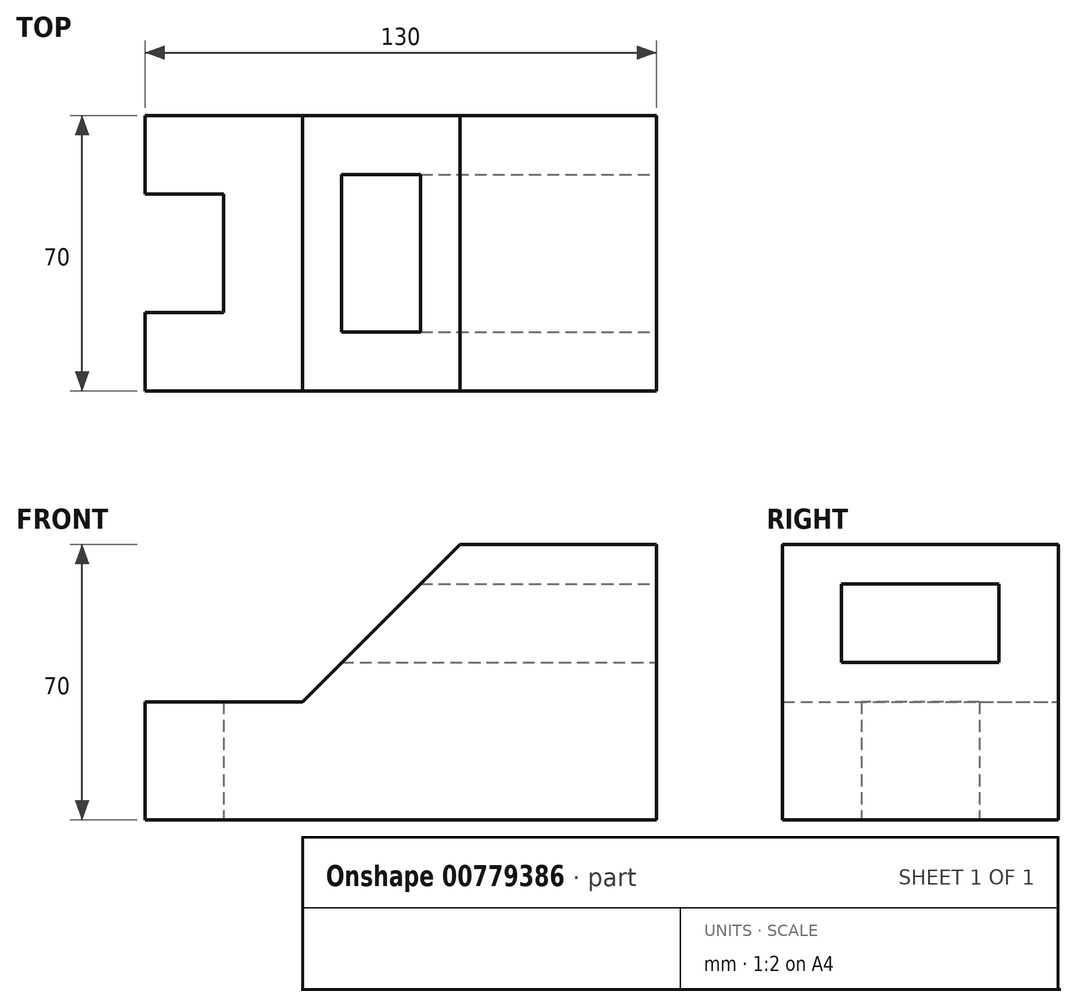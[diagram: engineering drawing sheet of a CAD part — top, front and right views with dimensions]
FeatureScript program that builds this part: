
annotation { "Feature Type Name" : "Feature", "Feature Type Description" : "" }
export const myFeature = defineFeature(function(context is Context, id is Id, definition is map)
    precondition{}
    {
        {
            var Q0;
            Q0=qCreatedBy(makeId("Front.planeOp"),FACE);
            var sketch = newSketch(context, id + "F0", { "sketchPlane" : qUnion([Q0])});
            skLineSegment(sketch, "E0.bottom", {"start": v(65, 35) * mm, "end": v(15, 35) * mm});
            skLineSegment(sketch, "E0.top", {"start": v(65, -35) * mm, "end": v(-65, -35) * mm});
            skLineSegment(sketch, "E0.left", {"start": v(65, 35) * mm, "end": v(65, -35) * mm});
            skLineSegment(sketch, "E0.right", {"start": v(-65, -5) * mm, "end": v(-65, -35) * mm});
            skPoint(sketch, "E0.middle", {"position": v(0, 0) * mm});
            skLineSegment(sketch, "E1.bottom", {"start": v(-65, -35) * mm, "end": v(-25, -35) * mm});
            skLineSegment(sketch, "E1.top", {"start": v(-65, -5) * mm, "end": v(-25, -5) * mm});
            skLineSegment(sketch, "E1.left", {"start": v(-65, -35) * mm, "end": v(-65, -5) * mm});
            skLineSegment(sketch, "E2", {"start": v(-25, -5) * mm, "end": v(15, 35) * mm});
            skPoint(sketch, "E3.orphan", {"position": v(-65, 35) * mm});
            skSolve(sketch);
        }
        {
            var Q0;
            Q0 = qSketchRegion(id + "F0", true);
            extrude(context, id + "F1", {"entities" : qUnion([Q0]), "depth" : 70 * mm, "offsetDistance" : 25 * mm});
        }
        {
            var Q0;
            Q0=makeQuery(id+"F1.opExtrude","SWEPT_FACE",FACE,{"disambiguationData":[OSD([sQuery(id+"F0.wireOp",EDGE,"E0.top"),sQuery(id+"F0.wireOp",EDGE,"E1.bottom")])]});
            var sketch = newSketch(context, id + "F2", { "sketchPlane" : qUnion([Q0])});
            skLineSegment(sketch, "E4.bottom", {"start": v(-65, 70) * mm, "end": v(-45, 70) * mm});
            skLineSegment(sketch, "E4.top", {"start": v(-65, 50) * mm, "end": v(-45, 50) * mm});
            skLineSegment(sketch, "E4.left", {"start": v(-65, 70) * mm, "end": v(-65, 50) * mm});
            skLineSegment(sketch, "E4.right", {"start": v(-45, 70) * mm, "end": v(-45, 50) * mm});
            skLineSegment(sketch, "E5.bottom", {"start": v(-65, 0) * mm, "end": v(-45, 0) * mm});
            skLineSegment(sketch, "E5.top", {"start": v(-65, 20) * mm, "end": v(-45, 20) * mm});
            skLineSegment(sketch, "E5.left", {"start": v(-65, 0) * mm, "end": v(-65, 20) * mm});
            skLineSegment(sketch, "E5.right", {"start": v(-45, 0) * mm, "end": v(-45, 20) * mm});
            skLineSegment(sketch, "E6", {"start": v(-45, 50) * mm, "end": v(-45, 20) * mm});
            skSolve(sketch);
        }
        {
            var Q0;
            {var subQ0=sQuery(id+"F2.wireOp",EDGE,"E4.top");Q0=makeQuery(id+"F2.imprint","IMPRINT",FACE,{"disambiguationData":[TD([[makeQuery(id+"F2.imprint","IMPRINT",EDGE,{"derivedFrom":subQ0}),-1.0]])]});}
            extrude(context, id + "F3", {"entities" : qUnion([Q0]), "operationType" : NewBodyOperationType.REMOVE, "endBound" : BoundingType.THROUGH_ALL, "oppositeDirection" : true, "depth" : 25 * mm, "offsetDistance" : 25 * mm});
        }
        {
            var Q0;
            Q0=makeQuery(id+"F1.opExtrude","SWEPT_FACE",FACE,{"disambiguationData":[OSD([sQuery(id+"F0.wireOp",EDGE,"E0.left")])]});
            var sketch = newSketch(context, id + "F4", { "sketchPlane" : qUnion([Q0])});
            skLineSegment(sketch, "E7.bottom", {"start": v(0, 35) * mm, "end": v(-15, 35) * mm});
            skLineSegment(sketch, "E7.top", {"start": v(0, 25) * mm, "end": v(-15, 25) * mm});
            skLineSegment(sketch, "E7.left", {"start": v(0, 35) * mm, "end": v(0, 25) * mm});
            skLineSegment(sketch, "E7.right", {"start": v(-15, 35) * mm, "end": v(-15, 25) * mm});
            skLineSegment(sketch, "E8.bottom", {"start": v(-70, 35) * mm, "end": v(-55, 35) * mm});
            skLineSegment(sketch, "E8.top", {"start": v(-70, 25) * mm, "end": v(-55, 25) * mm});
            skLineSegment(sketch, "E8.left", {"start": v(-70, 35) * mm, "end": v(-70, 25) * mm});
            skLineSegment(sketch, "E8.right", {"start": v(-55, 35) * mm, "end": v(-55, 25) * mm});
            skLineSegment(sketch, "E9", {"start": v(-55, 25) * mm, "end": v(-15, 25) * mm});
            skLineSegment(sketch, "E10", {"start": v(-55, 25) * mm, "end": v(-55, 5) * mm});
            skLineSegment(sketch, "E11", {"start": v(-15, 25) * mm, "end": v(-15, 5) * mm});
            skLineSegment(sketch, "E12", {"start": v(-55, 5) * mm, "end": v(-15, 5) * mm});
            skSolve(sketch);
        }
        {
            var Q0;
            Q0=makeQuery(id+"F4.imprint","IMPRINT",FACE,{"disambiguationData":[TD([[makeQuery(id+"F4.imprint","IMPRINT",EDGE,{"derivedFrom":sQuery(id+"F4.wireOp",EDGE,"E9")}),-1.0]])]});
            extrude(context, id + "F5", {"entities" : qUnion([Q0]), "operationType" : NewBodyOperationType.REMOVE, "endBound" : BoundingType.THROUGH_ALL, "oppositeDirection" : true, "depth" : 25 * mm, "offsetDistance" : 25 * mm});
        }
    });
